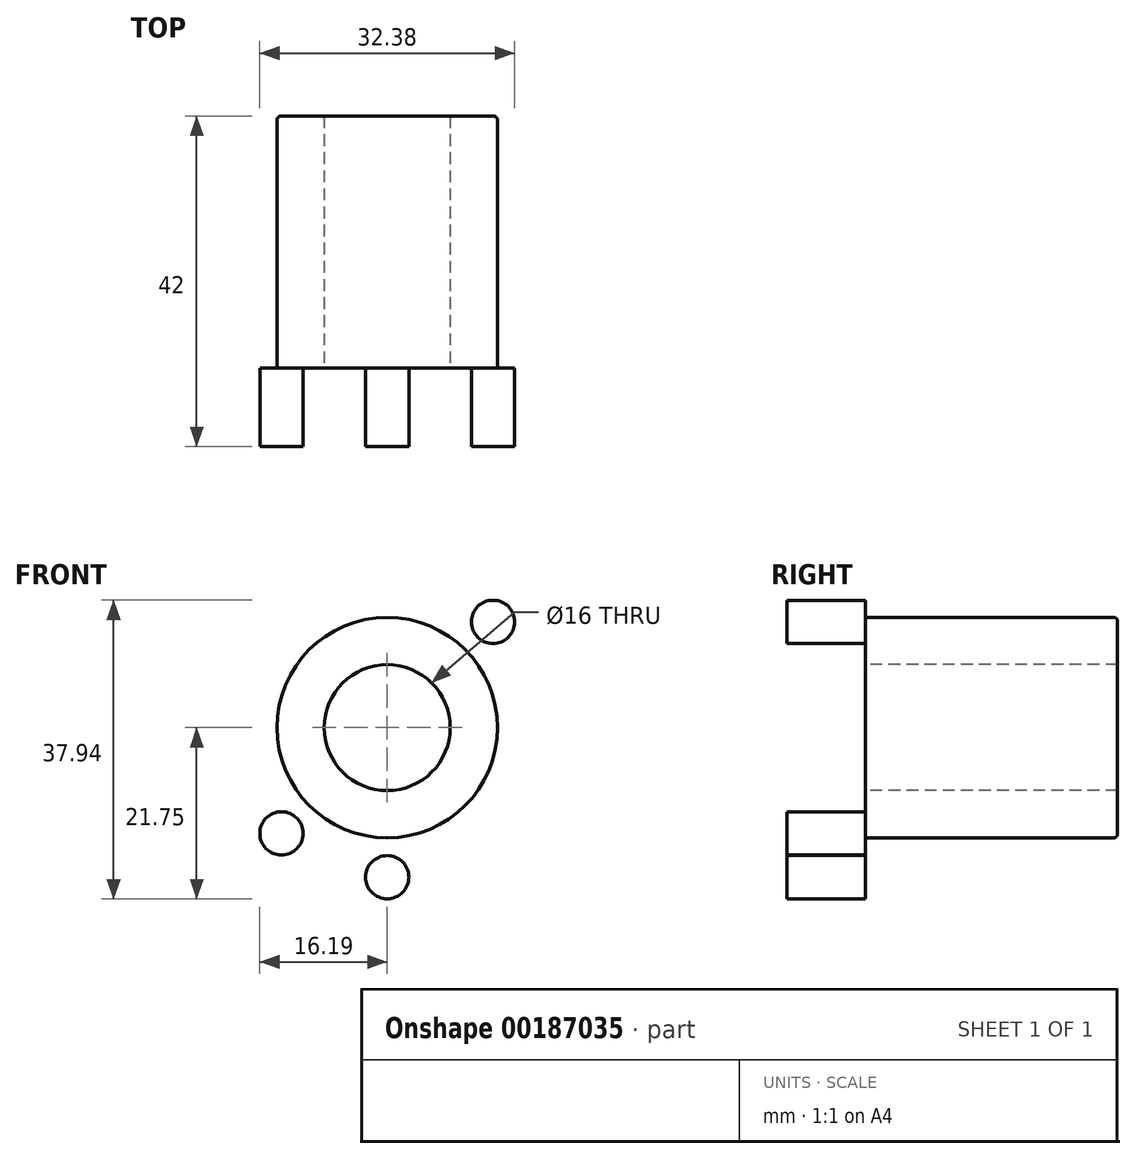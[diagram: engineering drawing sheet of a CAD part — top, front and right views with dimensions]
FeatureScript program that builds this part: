
annotation { "Feature Type Name" : "Feature", "Feature Type Description" : "" }
export const myFeature = defineFeature(function(context is Context, id is Id, definition is map)
    precondition{}
    {
        {
            var Q0;
            Q0=qCreatedBy(makeId("Front.planeOp"),FACE);
            var sketch = newSketch(context, id + "F0", { "sketchPlane" : qUnion([Q0])});
            skArc(sketch, "E0", {"start": v(-20.5, -12.48) * mm, "mid": v(0, -24) * mm, "end": v(20.5, -12.48) * mm});
            skLineSegment(sketch, "E1", {"start": v(-20.5, 12.48) * mm, "end": v(-20.5, -12.48) * mm});
            skLineSegment(sketch, "E2", {"start": v(20.5, 12.48) * mm, "end": v(20.5, -12.48) * mm});
            skArc(sketch, "E3.trimOffspring", {"start": v(20.5, 12.48) * mm, "mid": v(0, 24) * mm, "end": v(-20.5, 12.48) * mm});
            skSolve(sketch);
        }
        {
            var Q0;
            Q0=makeQuery(id+"F0.imprint","IMPRINT",FACE,{"disambiguationData":[TD([[makeQuery(id+"F0.imprint","IMPRINT",EDGE,{"derivedFrom":sQuery(id+"F0.wireOp",EDGE,"E0")}),1.0]])]});
            extrude(context, id + "F1", {"entities" : qUnion([Q0]), "depth" : 10 * mm});
        }
        {
            var Q0;
            Q0=makeQuery(id+"F1.opExtrude","CAP_FACE",FACE,{"disambiguationData":[OSD([sQuery(id+"F0.wireOp",EDGE,"E0"),sQuery(id+"F0.wireOp",EDGE,"E1"),sQuery(id+"F0.wireOp",EDGE,"E2"),sQuery(id+"F0.wireOp",EDGE,"E3.trimOffspring")])],"isStart":false});
            var sketch = newSketch(context, id + "F2", { "sketchPlane" : qUnion([Q0])});
            skCircle(sketch, "E4", {"center": v(0, 19) * mm, "radius": 2.75 * mm});
            skCircle(sketch, "E5", {"center": v(0, 0) * mm, "radius": 19 * mm, "construction": true});
            skCircle(sketch, "E6", {"center": v(-13.44, 13.44) * mm, "radius": 2.75 * mm});
            skLineSegment(sketch, "E7", {"start": v(-13.44, 13.44) * mm, "end": v(0, 0) * mm, "construction": true});
            skLineSegment(sketch, "E8", {"start": v(0, 19) * mm, "end": v(0, 0) * mm, "construction": true});
            skCircle(sketch, "E9.MirrorC", {"center": v(13.44, 13.44) * mm, "radius": 2.75 * mm});
            skCircle(sketch, "E10.MirrorC", {"center": v(13.44, -13.44) * mm, "radius": 2.75 * mm});
            skCircle(sketch, "E11.MirrorC", {"center": v(0, -19) * mm, "radius": 2.75 * mm});
            skCircle(sketch, "E12.MirrorC", {"center": v(-13.44, -13.44) * mm, "radius": 2.75 * mm});
            skSolve(sketch);
        }
        {
            var Q0;
            Q0=makeQuery(id+"F2.imprint","IMPRINT",FACE,{"disambiguationData":[TD([[makeQuery(id+"F2.imprint","IMPRINT",EDGE,{"derivedFrom":sQuery(id+"F2.wireOp",EDGE,"E4")}),1.0]])]});
            var Q1;
            Q1=makeQuery(id+"F2.imprint","IMPRINT",FACE,{"disambiguationData":[TD([[makeQuery(id+"F2.imprint","IMPRINT",EDGE,{"derivedFrom":sQuery(id+"F2.wireOp",EDGE,"E6")}),1.0]])]});
            var Q2;
            Q2=makeQuery(id+"F2.imprint","IMPRINT",FACE,{"disambiguationData":[TD([[makeQuery(id+"F2.imprint","IMPRINT",EDGE,{"derivedFrom":sQuery(id+"F2.wireOp",EDGE,"E10.MirrorC")}),1.0]])]});
            var Q3;
            Q3=makeQuery(id+"F2.imprint","IMPRINT",FACE,{"disambiguationData":[TD([[makeQuery(id+"F2.imprint","IMPRINT",EDGE,{"derivedFrom":sQuery(id+"F2.wireOp",EDGE,"E9.MirrorC")}),-1.0]])]});
            var Q4;
            Q4=makeQuery(id+"F2.imprint","IMPRINT",FACE,{"disambiguationData":[TD([[makeQuery(id+"F2.imprint","IMPRINT",EDGE,{"derivedFrom":sQuery(id+"F2.wireOp",EDGE,"E12.MirrorC")}),-1.0]])]});
            var Q5;
            Q5=makeQuery(id+"F2.imprint","IMPRINT",FACE,{"disambiguationData":[TD([[makeQuery(id+"F2.imprint","IMPRINT",EDGE,{"derivedFrom":sQuery(id+"F2.wireOp",EDGE,"E11.MirrorC")}),-1.0]])]});
            var Q6;
            Q6=sQuery(id+"F2.wireOp",EDGE,"E4");
            extrude(context, id + "F3", {"entities" : qUnion([Q0, Q1, Q2, Q3, Q4, Q5]), "operationType" : NewBodyOperationType.REMOVE, "surfaceEntities" : qUnion([Q6]), "endBound" : BoundingType.THROUGH_ALL, "oppositeDirection" : true, "depth" : 25 * mm});
        }
        {
            var Q0;
            Q0=makeQuery(id+"F1.opExtrude","CAP_FACE",FACE,{"disambiguationData":[OSD([sQuery(id+"F0.wireOp",EDGE,"E0"),sQuery(id+"F0.wireOp",EDGE,"E1"),sQuery(id+"F0.wireOp",EDGE,"E2"),sQuery(id+"F0.wireOp",EDGE,"E3.trimOffspring")])],"isStart":true});
            var sketch = newSketch(context, id + "F4", { "sketchPlane" : qUnion([Q0])});
            skCircle(sketch, "E13", {"center": v(0, 0) * mm, "radius": 14 * mm});
            skSolve(sketch);
        }
        {
            var Q0;
            Q0=makeQuery(id+"F4.imprint","IMPRINT",FACE,{"disambiguationData":[TD([[makeQuery(id+"F4.imprint","IMPRINT",EDGE,{"derivedFrom":sQuery(id+"F4.wireOp",EDGE,"E13")}),1.0]])]});
            extrude(context, id + "F5", {"entities" : qUnion([Q0]), "operationType" : NewBodyOperationType.ADD, "depth" : 32 * mm});
        }
        {
            var Q0;
            Q0=makeQuery(id+"F1.opExtrude","CAP_FACE",FACE,{"disambiguationData":[OSD([sQuery(id+"F0.wireOp",EDGE,"E0"),sQuery(id+"F0.wireOp",EDGE,"E1"),sQuery(id+"F0.wireOp",EDGE,"E2"),sQuery(id+"F0.wireOp",EDGE,"E3.trimOffspring")])],"isStart":false});
            var sketch = newSketch(context, id + "F6", { "sketchPlane" : qUnion([Q0])});
            skCircle(sketch, "E14", {"center": v(0, 0) * mm, "radius": 8 * mm});
            skSolve(sketch);
        }
        {
            var Q0;
            Q0=makeQuery(id+"F6.imprint","IMPRINT",FACE,{"disambiguationData":[TD([[makeQuery(id+"F6.imprint","IMPRINT",EDGE,{"derivedFrom":sQuery(id+"F6.wireOp",EDGE,"E14")}),1.0]])]});
            extrude(context, id + "F7", {"entities" : qUnion([Q0]), "operationType" : NewBodyOperationType.REMOVE, "endBound" : BoundingType.THROUGH_ALL, "oppositeDirection" : true, "depth" : 25 * mm});
        }
        {
            var Q0;
            Q0=makeQuery(id+"F5.opExtrude","CAP_EDGE",EDGE,{"disambiguationData":[OSD([sQuery(id+"F4.wireOp",EDGE,"E13")])],"isStart":false});
            var Q1;
            Q1=makeQuery(id+"F1.opExtrude","CAP_EDGE",EDGE,{"disambiguationData":[OSD([sQuery(id+"F0.wireOp",EDGE,"E3.trimOffspring")])],"isStart":true});
            var Q2;
            Q2=makeQuery(id+"F1.opExtrude","CAP_EDGE",EDGE,{"disambiguationData":[OSD([sQuery(id+"F0.wireOp",EDGE,"E0")])],"isStart":true});
            var Q3;
            Q3=makeQuery(id+"F1.opExtrude","CAP_EDGE",EDGE,{"disambiguationData":[OSD([sQuery(id+"F0.wireOp",EDGE,"E0")])],"isStart":false});
            var Q4;
            Q4=makeQuery(id+"F1.opExtrude","CAP_EDGE",EDGE,{"disambiguationData":[OSD([sQuery(id+"F0.wireOp",EDGE,"E3.trimOffspring")])],"isStart":false});
            fillet(context, id + "F8", {"entities" : qUnion([Q0, Q1, Q2, Q3, Q4]), "radius" : .5 * mm, "tangentPropagation" : true, "allowEdgeOverflow" : false});
        }
    });
